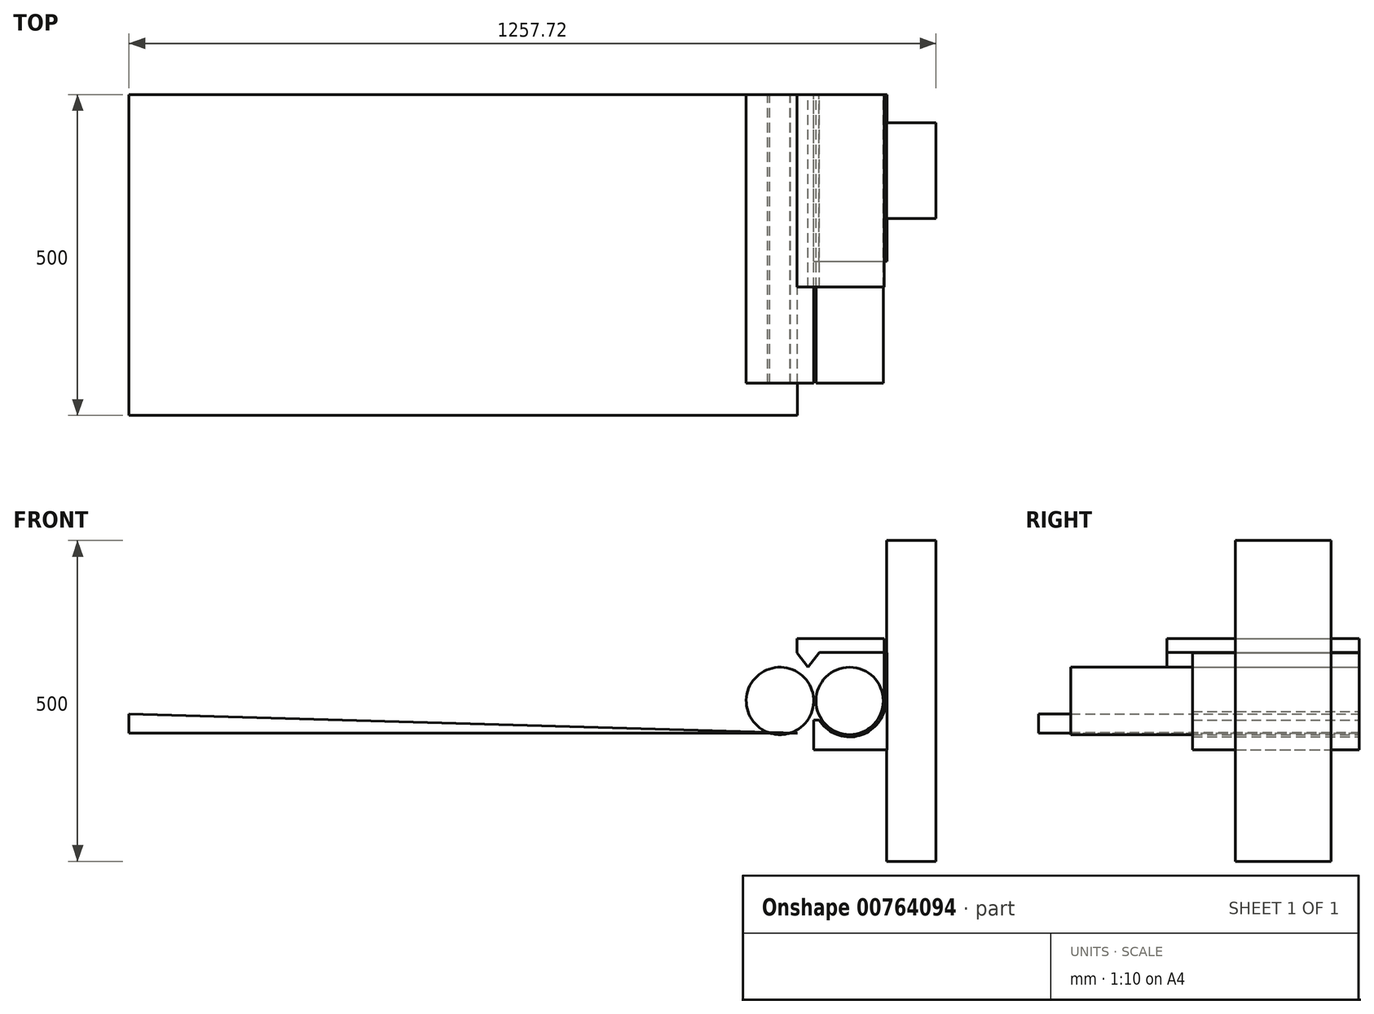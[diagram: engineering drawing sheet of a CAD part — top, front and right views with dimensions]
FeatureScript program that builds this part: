
annotation { "Feature Type Name" : "Feature", "Feature Type Description" : "" }
export const myFeature = defineFeature(function(context is Context, id is Id, definition is map)
    precondition{}
    {
        {
            var Q0;
            Q0=qCreatedBy(makeId("Front.planeOp"),FACE);
            var sketch = newSketch(context, id + "F0", { "sketchPlane" : qUnion([Q0])});
            skCircle(sketch, "E0", {"center": v(0, 0) * mm, "radius": 52.5 * mm});
            skSolve(sketch);
        }
        {
            var Q0;
            Q0 = qSketchRegion(id + "F0", true);
            extrude(context, id + "F1", {"entities" : qUnion([Q0]), "depth" : 450 * mm, "offsetDistance" : 25 * mm});
        }
        {
            var Q0;
            Q0=qCreatedBy(makeId("Front.planeOp"),FACE);
            var sketch = newSketch(context, id + "F2", { "sketchPlane" : qUnion([Q0])});
            skLineSegment(sketch, "E1", {"start": v(-56.1, -76.07) * mm, "end": v(51.9, -76.07) * mm});
            skArc(sketch, "E2", {"start": v(-47.6, -29.7) * mm, "mid": v(7.3, -55.63) * mm, "end": v(53.64, -16.43) * mm});
            skLineSegment(sketch, "E3", {"start": v(-56.1, -29.7) * mm, "end": v(-56.1, -76.07) * mm});
            skLineSegment(sketch, "E4", {"start": v(-56.1, -29.7) * mm, "end": v(-47.6, -29.7) * mm});
            skPoint(sketch, "E5.orphan", {"position": v(-56.1, 0) * mm});
            skLineSegment(sketch, "E6", {"start": v(58.44, 74) * mm, "end": v(58.44, -76.07) * mm});
            skLineSegment(sketch, "E7", {"start": v(58.44, -76.07) * mm, "end": v(51.9, -76.07) * mm});
            skPoint(sketch, "E8.end.orphan", {"position": v(56, 0) * mm});
            skLineSegment(sketch, "E9", {"start": v(53.64, -16.43) * mm, "end": v(53.64, 75.16) * mm});
            skLineSegment(sketch, "E10", {"start": v(53.64, 75.16) * mm, "end": v(58.44, 75.16) * mm});
            skLineSegment(sketch, "E11", {"start": v(58.44, 75.16) * mm, "end": v(58.44, 74) * mm});
            skLineSegment(sketch, "E12", {"start": v(-51.85, -29.7) * mm, "end": v(-51.85, 75.3) * mm});
            skSolve(sketch);
        }
        {
            var Q0;
            {var subQ0=sQuery(id+"F2.wireOp",EDGE,"E1");Q0=makeQuery(id+"F2.imprint","IMPRINT",FACE,{"disambiguationData":[TD([[makeQuery(id+"F2.imprint","IMPRINT",EDGE,{"derivedFrom":subQ0}),1.0]])]});}
            extrude(context, id + "F3", {"entities" : qUnion([Q0]), "depth" : 260 * mm, "offsetDistance" : 25 * mm});
        }
        {
            var Q0;
            Q0=qCreatedBy(makeId("Top.planeOp"),FACE);
            var sketch = newSketch(context, id + "F4", { "sketchPlane" : qUnion([Q0])});
            skLineSegment(sketch, "E13.bottom", {"start": v(57.55, -193.01) * mm, "end": v(134.49, -193.01) * mm});
            skLineSegment(sketch, "E13.top", {"start": v(57.55, -44.23) * mm, "end": v(134.49, -44.23) * mm});
            skLineSegment(sketch, "E13.left", {"start": v(57.55, -193.01) * mm, "end": v(57.55, -44.23) * mm});
            skLineSegment(sketch, "E13.right", {"start": v(134.49, -193.01) * mm, "end": v(134.49, -44.23) * mm});
            skSolve(sketch);
        }
        {
            var Q0;
            Q0=makeQuery(id+"F4.imprint","IMPRINT",FACE,{"disambiguationData":[TD([[makeQuery(id+"F4.imprint","IMPRINT",EDGE,{"derivedFrom":sQuery(id+"F4.wireOp",EDGE,"E13.bottom")}),1.0]])]});
            extrude(context, id + "F5", {"entities" : qUnion([Q0]), "endBound" : BoundingType.SYMMETRIC, "depth" : 500 * mm, "offsetDistance" : 25 * mm});
        }
        {
            var Q0;
            Q0=qCreatedBy(makeId("Front.planeOp"),FACE);
            var sketch = newSketch(context, id + "F6", { "sketchPlane" : qUnion([Q0])});
            skLineSegment(sketch, "E14", {"start": v(-81.46, -50.1) * mm, "end": v(-1123.23, -50.1) * mm});
            skLineSegment(sketch, "E15", {"start": v(-1123.23, -50.1) * mm, "end": v(-1123.23, -20.08) * mm});
            skLineSegment(sketch, "E16", {"start": v(-1123.23, -20.08) * mm, "end": v(-81.46, -50.1) * mm});
            skSolve(sketch);
        }
        {
            var Q0;
            Q0 = qSketchRegion(id + "F6", true);
            extrude(context, id + "F7", {"entities" : qUnion([Q0]), "depth" : 500 * mm, "offsetDistance" : 25 * mm});
        }
        {
            var Q0;
            Q0=qCreatedBy(makeId("Front.planeOp"),FACE);
            var sketch = newSketch(context, id + "F8", { "sketchPlane" : qUnion([Q0])});
            skLineSegment(sketch, "E17", {"start": v(-55.64, 0) * mm, "end": v(-108.64, 0) * mm});
            skCircle(sketch, "E18", {"center": v(-108.64, 0) * mm, "radius": 52.5 * mm});
            skSolve(sketch);
        }
        {
            var Q0;
            Q0=makeQuery(id+"F8.imprint","IMPRINT",FACE,{"disambiguationData":[TD([[makeQuery(id+"F8.imprint","IMPRINT",EDGE,{"derivedFrom":sQuery(id+"F8.wireOp",EDGE,"E18")}),1.0]])]});
            extrude(context, id + "F9", {"entities" : qUnion([Q0]), "operationType" : NewBodyOperationType.ADD, "depth" : 450 * mm, "offsetDistance" : 25 * mm});
        }
        {
            var Q0;
            Q0=qCreatedBy(makeId("Front.planeOp"),FACE);
            var sketch = newSketch(context, id + "F10", { "sketchPlane" : qUnion([Q0])});
            skLineSegment(sketch, "E19", {"start": v(-82.04, 75.16) * mm, "end": v(-65.16, 52.35) * mm});
            skLineSegment(sketch, "E20", {"start": v(-65.16, 52.35) * mm, "end": v(-47.36, 75.62) * mm});
            skLineSegment(sketch, "E21", {"start": v(-47.36, 75.62) * mm, "end": v(-82.04, 75.16) * mm});
            skLineSegment(sketch, "E22", {"start": v(-82.04, 75.16) * mm, "end": v(-82.33, 97.04) * mm});
            skLineSegment(sketch, "E23", {"start": v(-82.33, 97.04) * mm, "end": v(53.94, 97.04) * mm});
            skLineSegment(sketch, "E24", {"start": v(53.94, 97.04) * mm, "end": v(53.94, 75.62) * mm});
            skLineSegment(sketch, "E25", {"start": v(53.94, 75.62) * mm, "end": v(-47.36, 75.62) * mm});
            skSolve(sketch);
        }
        {
            var Q0;
            Q0=makeQuery(id+"F10.imprint","IMPRINT",FACE,{"disambiguationData":[TD([[makeQuery(id+"F10.imprint","IMPRINT",EDGE,{"derivedFrom":sQuery(id+"F10.wireOp",EDGE,"E19")}),1.0]])]});
            var Q1;
            Q1=makeQuery(id+"F10.imprint","IMPRINT",FACE,{"disambiguationData":[TD([[makeQuery(id+"F10.imprint","IMPRINT",EDGE,{"derivedFrom":sQuery(id+"F10.wireOp",EDGE,"E21")}),-1.0]])]});
            extrude(context, id + "F11", {"entities" : qUnion([Q0, Q1]), "depth" : 300 * mm, "offsetDistance" : 25 * mm});
        }
    });
